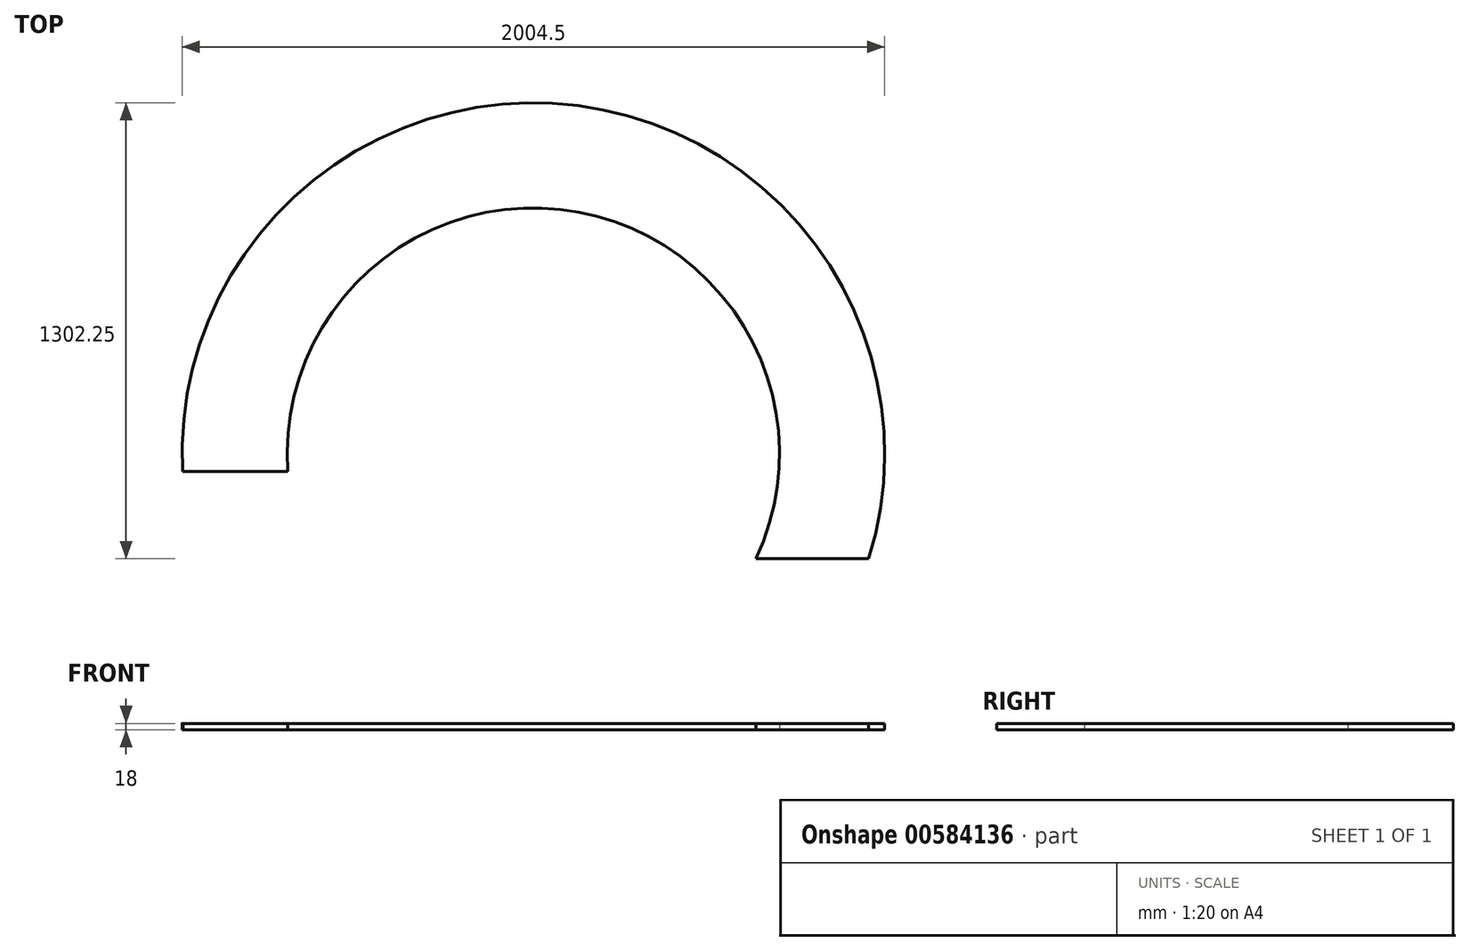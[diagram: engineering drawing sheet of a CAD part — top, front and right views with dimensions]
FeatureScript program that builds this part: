
annotation { "Feature Type Name" : "Feature", "Feature Type Description" : "" }
export const myFeature = defineFeature(function(context is Context, id is Id, definition is map)
    precondition{}
    {
        {
            var Q0;
            Q0=qCreatedBy(makeId("Top.planeOp"),FACE);
            var sketch = newSketch(context, id + "F0", { "sketchPlane" : qUnion([Q0])});
            skArc(sketch, "E0", {"start": v(634.94, -300) * mm, "mid": v(129.22, 690.26) * mm, "end": v(-700.47, -50) * mm});
            skLineSegment(sketch, "E1", {"start": v(-363.1, -173.08) * mm, "end": v(-364.33, -173.66) * mm});
            skArc(sketch, "E2.0", {"start": v(956.3, -300) * mm, "mid": v(126.97, 994.17) * mm, "end": v(-1001, -50.04) * mm});
            skLineSegment(sketch, "E3", {"start": v(634.94, -300) * mm, "end": v(956.3, -300) * mm});
            skLineSegment(sketch, "E4", {"start": v(-700.47, -50) * mm, "end": v(-999.7, -50) * mm});
            skLineSegment(sketch, "E5", {"start": v(-999.7, -50) * mm, "end": v(-1001, -50.04) * mm});
            skPoint(sketch, "E6.orphan", {"position": v(-999.7, -71.36) * mm});
            skSolve(sketch);
        }
        {
            var Q0;
            Q0 = qSketchRegion(id + "F0", true);
            extrude(context, id + "F1", {"entities" : qUnion([Q0]), "depth" : 18 * mm, "offsetDistance" : 25 * mm});
        }
    });
